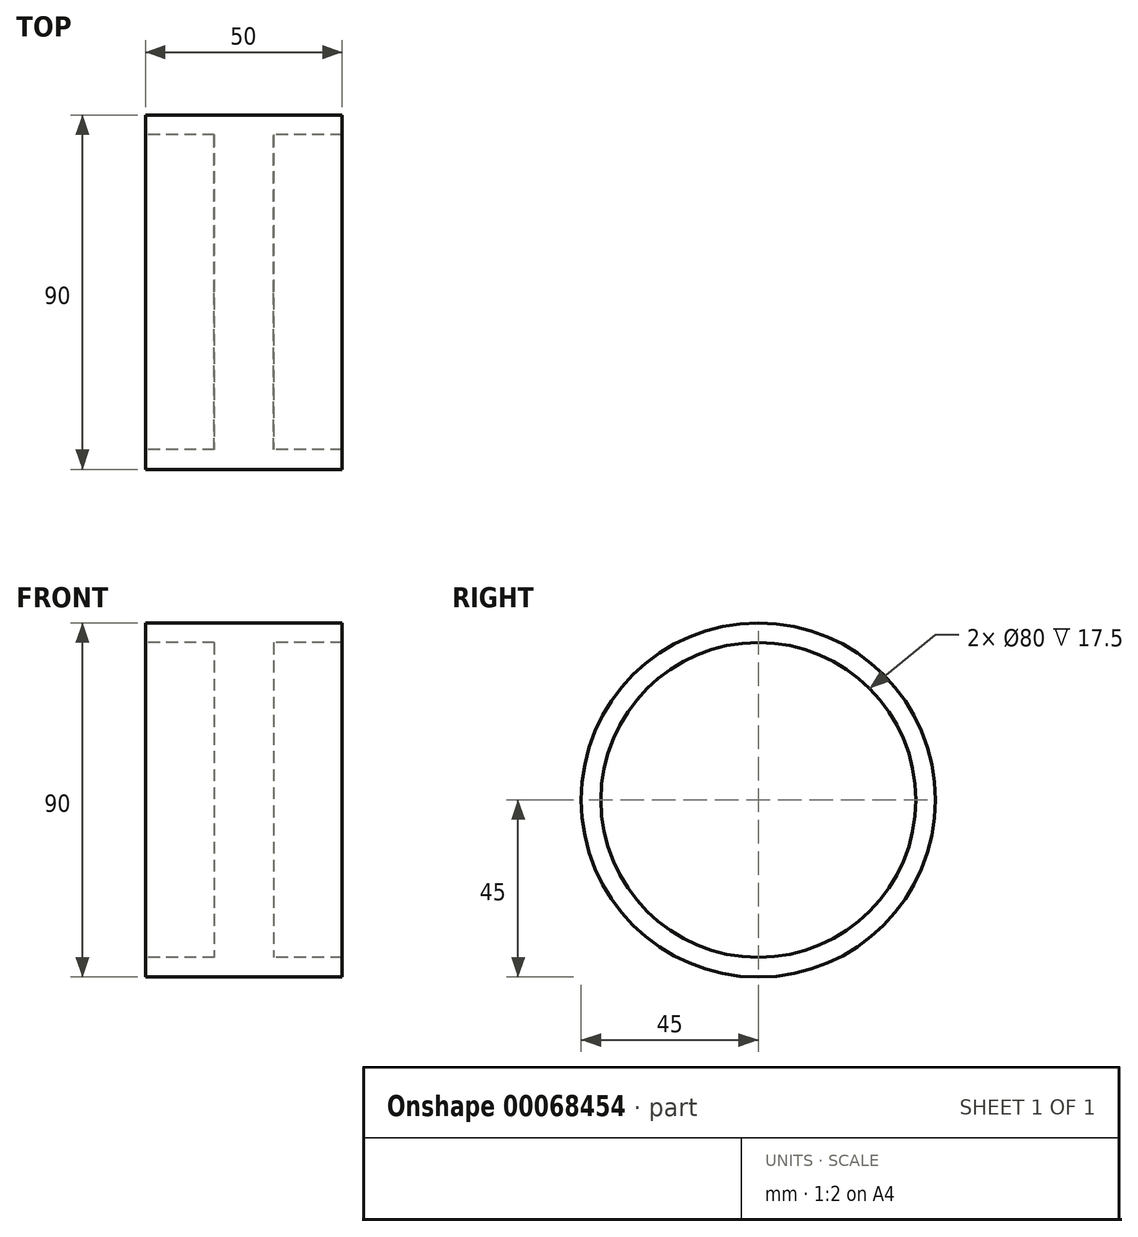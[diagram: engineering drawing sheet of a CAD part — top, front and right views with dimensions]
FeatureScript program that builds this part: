
annotation { "Feature Type Name" : "Feature", "Feature Type Description" : "" }
export const myFeature = defineFeature(function(context is Context, id is Id, definition is map)
    precondition{}
    {
        {
            var Q0;
            Q0=qCreatedBy(makeId("Front.planeOp"),FACE);
            var sketch = newSketch(context, id + "F0", { "sketchPlane" : qUnion([Q0])});
            skLineSegment(sketch, "E0.bottom", {"start": v(-7.5, 40) * mm, "end": v(7.5, 40) * mm});
            skLineSegment(sketch, "E0.top", {"start": v(-7.5, 0) * mm, "end": v(7.5, 0) * mm});
            skLineSegment(sketch, "E0.left", {"start": v(-7.5, 40) * mm, "end": v(-7.5, 0) * mm});
            skLineSegment(sketch, "E0.right", {"start": v(7.5, 40) * mm, "end": v(7.5, 0) * mm});
            skLineSegment(sketch, "E1.bottom", {"start": v(-25, 45) * mm, "end": v(25, 45) * mm});
            skLineSegment(sketch, "E1.top", {"start": v(-25, 40) * mm, "end": v(25, 40) * mm});
            skLineSegment(sketch, "E1.left", {"start": v(25, 45) * mm, "end": v(25, 40) * mm});
            skLineSegment(sketch, "E1.right", {"start": v(-25, 45) * mm, "end": v(-25, 40) * mm});
            skPoint(sketch, "E2", {"position": v(0, 40) * mm});
            skPoint(sketch, "E3", {"position": v(0, 0) * mm});
            skSolve(sketch);
        }
        {
            var Q0;
            Q0=makeQuery(id+"F0.imprint","IMPRINT",FACE,{"disambiguationData":[TD([[makeQuery(id+"F0.imprint","IMPRINT",EDGE,{"derivedFrom":sQuery(id+"F0.wireOp",EDGE,"E0.top")}),1.0]])]});
            var Q1;
            Q1=makeQuery(id+"F0.imprint","IMPRINT",FACE,{"disambiguationData":[TD([[makeQuery(id+"F0.imprint","IMPRINT",EDGE,{"derivedFrom":sQuery(id+"F0.wireOp",EDGE,"E1.bottom")}),-1.0]])]});
            var Q2;
            Q2=sQuery(id+"F0.wireOp",EDGE,"E0.top");
            revolve(context, id + "F1", {"entities" : qUnion([Q0, Q1]), "axis" : qUnion([Q2]), "revolveType" : RevolveType.FULL});
        }
    });
